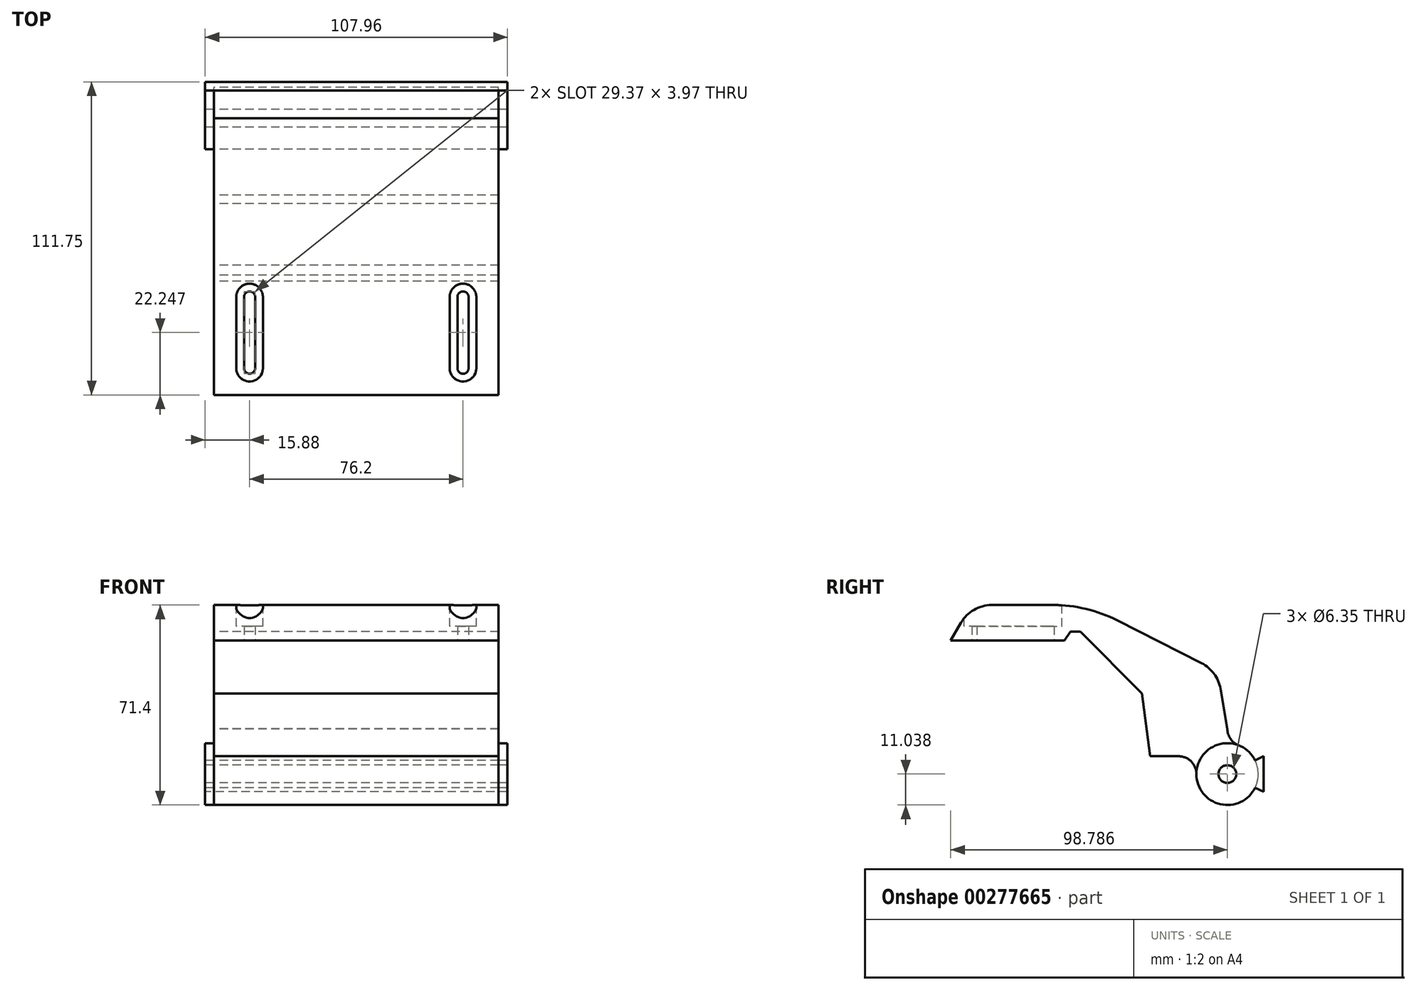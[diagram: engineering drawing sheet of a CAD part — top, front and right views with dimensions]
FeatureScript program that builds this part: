
annotation { "Feature Type Name" : "Feature", "Feature Type Description" : "" }
export const myFeature = defineFeature(function(context is Context, id is Id, definition is map)
    precondition{}
    {
        {
            var Q0;
            Q0=qCreatedBy(makeId("Right.planeOp"),FACE);
            var sketch = newSketch(context, id + "F0", { "sketchPlane" : qUnion([Q0])});
            skLineSegment(sketch, "E0", {"start": v(-105.67, 0) * mm, "end": v(-65.03, 0) * mm});
            skLineSegment(sketch, "E1", {"start": v(-65.03, 0) * mm, "end": v(-62.9, 3.18) * mm});
            skLineSegment(sketch, "E2", {"start": v(-62.9, 3.18) * mm, "end": v(-59.37, 3.18) * mm});
            skLineSegment(sketch, "E3", {"start": v(-59.37, 3.18) * mm, "end": v(-37.35, -18.84) * mm});
            skLineSegment(sketch, "E4", {"start": v(-37.35, -18.84) * mm, "end": v(-34.4, -41.3) * mm});
            skSolve(sketch);
        }
        {
            var Q0;
            Q0=sQuery(id+"F0.wireOp",EDGE,"E0");
            var Q1;
            Q1=sQuery(id+"F0.wireOp",EDGE,"E1");
            var Q2;
            Q2=sQuery(id+"F0.wireOp",EDGE,"E2");
            var Q3;
            Q3=sQuery(id+"F0.wireOp",EDGE,"E3");
            var Q4;
            Q4=sQuery(id+"F0.wireOp",EDGE,"E4");
            extrude(context, id + "F1", {"bodyType" : ToolBodyType.SURFACE, "surfaceEntities" : qUnion([Q0, Q1, Q2, Q3, Q4]), "depth" : 73.02 * mm, "hasSecondDirection" : true, "secondDirectionOppositeDirection" : true, "secondDirectionDepth" : 73.02 * mm});
        }
        {
            var Q0;
            Q0=qCreatedBy(makeId("Right.planeOp"),FACE);
            var sketch = newSketch(context, id + "F2", { "sketchPlane" : qUnion([Q0])});
            skLineSegment(sketch, "E5.0", {"start": v(-105.67, 0) * mm, "end": v(-65.03, 0) * mm});
            skLineSegment(sketch, "E6", {"start": v(-105.67, 0) * mm, "end": v(-98.34, 12.7) * mm});
            skLineSegment(sketch, "E7", {"start": v(-98.34, 12.7) * mm, "end": v(-57.06, 12.7) * mm});
            skLineSegment(sketch, "E8", {"start": v(-57.06, 12.7) * mm, "end": v(-10.39, -10.96) * mm});
            skLineSegment(sketch, "E9.0.0", {"start": v(-62.9, 3.18) * mm, "end": v(-65.03, 0) * mm});
            skLineSegment(sketch, "E9.0.2", {"start": v(-65.03, 0) * mm, "end": v(-62.9, 3.18) * mm});
            skLineSegment(sketch, "E10.0.0", {"start": v(-59.37, 3.18) * mm, "end": v(-62.9, 3.18) * mm});
            skLineSegment(sketch, "E10.0.2", {"start": v(-62.9, 3.18) * mm, "end": v(-59.37, 3.18) * mm});
            skLineSegment(sketch, "E11.0.0", {"start": v(-37.35, -18.84) * mm, "end": v(-59.37, 3.18) * mm});
            skLineSegment(sketch, "E11.0.2", {"start": v(-59.37, 3.18) * mm, "end": v(-37.35, -18.84) * mm});
            skLineSegment(sketch, "E12.0.0", {"start": v(-34.4, -41.3) * mm, "end": v(-37.35, -18.84) * mm});
            skLineSegment(sketch, "E12.0.2", {"start": v(-37.35, -18.84) * mm, "end": v(-34.4, -41.3) * mm});
            skLineSegment(sketch, "E13", {"start": v(-34.4, -41.3) * mm, "end": v(-21.7, -41.3) * mm});
            skArc(sketch, "E14", {"start": v(-6.88, -31.54) * mm, "mid": v(-15.75, -34.2) * mm, "end": v(-21.7, -41.3) * mm});
            skLineSegment(sketch, "E15", {"start": v(-6.88, -31.54) * mm, "end": v(-10.39, -10.96) * mm});
            skSolve(sketch);
        }
        {
            var Q0;
            Q0 = qSketchRegion(id + "F2", true);
            extrude(context, id + "F3", {"entities" : qUnion([Q0]), "endBound" : BoundingType.SYMMETRIC, "depth" : 101.6 * mm});
        }
        {
            var Q0;
            Q0=qCreatedBy(makeId("Right.planeOp"),FACE);
            var sketch = newSketch(context, id + "F4", { "sketchPlane" : qUnion([Q0])});
            skArc(sketch, "E16.0", {"start": v(-6.88, -31.54) * mm, "mid": v(-15.75, -34.2) * mm, "end": v(-21.7, -41.3) * mm});
            skLineSegment(sketch, "E17", {"start": v(-6.88, -31.47) * mm, "end": v(-6.88, -31.54) * mm});
            skLineSegment(sketch, "E18", {"start": v(-24.27, -41.3) * mm, "end": v(-21.7, -41.3) * mm});
            skArc(sketch, "E19", {"start": v(-17.92, -47.66) * mm, "mid": v(-0.67, -56.78) * mm, "end": v(-2.85, -37.39) * mm});
            skCircle(sketch, "E20", {"center": v(-6.88, -47.66) * mm, "radius": 3.18 * mm});
            skPoint(sketch, "E21.visualSharp", {"position": v(-6.88, -36.62) * mm});
            skArc(sketch, "E21.filletArc", {"start": v(-6.88, -31.47) * mm, "mid": v(-5.78, -35.05) * mm, "end": v(-2.85, -37.39) * mm});
            skPoint(sketch, "E22.visualSharp", {"position": v(-15.91, -41.3) * mm});
            skArc(sketch, "E22.filletArc", {"start": v(-17.92, -47.66) * mm, "mid": v(-19.78, -43.17) * mm, "end": v(-24.27, -41.3) * mm});
            skSolve(sketch);
        }
        {
            var Q0;
            Q0=makeQuery(id+"F4.imprint","IMPRINT",FACE,{"disambiguationData":[TD([[makeQuery(id+"F4.imprint","IMPRINT",EDGE,{"derivedFrom":sQuery(id+"F4.wireOp",EDGE,"E16.0")}),1.0]])]});
            var Q1;
            Q1=makeQuery(id+"F3.opExtrude","CAP_FACE",FACE,{"disambiguationData":[OSD([sQuery(id+"F2.wireOp",EDGE,"E5.0"),sQuery(id+"F2.wireOp",EDGE,"E6"),sQuery(id+"F2.wireOp",EDGE,"E7"),sQuery(id+"F2.wireOp",EDGE,"E8"),sQuery(id+"F2.wireOp",EDGE,"E9.0.2"),sQuery(id+"F2.wireOp",EDGE,"E10.0.2"),sQuery(id+"F2.wireOp",EDGE,"E11.0.2"),sQuery(id+"F2.wireOp",EDGE,"E12.0.2"),sQuery(id+"F2.wireOp",EDGE,"E13"),sQuery(id+"F2.wireOp",EDGE,"E14"),sQuery(id+"F2.wireOp",EDGE,"E15")])],"isStart":false});
            var Q2;
            Q2=makeQuery(id+"F3.opExtrude","CAP_FACE",FACE,{"disambiguationData":[OSD([sQuery(id+"F2.wireOp",EDGE,"E5.0"),sQuery(id+"F2.wireOp",EDGE,"E6"),sQuery(id+"F2.wireOp",EDGE,"E7"),sQuery(id+"F2.wireOp",EDGE,"E8"),sQuery(id+"F2.wireOp",EDGE,"E9.0.2"),sQuery(id+"F2.wireOp",EDGE,"E10.0.2"),sQuery(id+"F2.wireOp",EDGE,"E11.0.2"),sQuery(id+"F2.wireOp",EDGE,"E12.0.2"),sQuery(id+"F2.wireOp",EDGE,"E13"),sQuery(id+"F2.wireOp",EDGE,"E14"),sQuery(id+"F2.wireOp",EDGE,"E15")])],"isStart":true});
            extrude(context, id + "F5", {"entities" : qUnion([Q0]), "operationType" : NewBodyOperationType.ADD, "endBound" : BoundingType.UP_TO_SURFACE, "endBoundEntityFace" : qUnion([Q1]), "depth" : 25.4 * mm, "hasSecondDirection" : true, "secondDirectionBound" : SecondDirectionBoundingType.UP_TO_SURFACE, "secondDirectionOppositeDirection" : true, "secondDirectionBoundEntityFace" : qUnion([Q2]), "secondDirectionDepth" : 25.4 * mm});
        }
        {
            var Q0;
            Q0=makeQuery(id+"F3.opExtrude","SWEPT_EDGE",EDGE,{"disambiguationData":[OSD([sQuery(id+"F2.wireOp",EDGE,"E7"),sQuery(id+"F2.wireOp",EDGE,"E8")])]});
            fillet(context, id + "F6", {"entities" : qUnion([Q0]), "radius" : 50.8 * mm, "tangentPropagation" : true, "allowEdgeOverflow" : false});
        }
        {
            var Q0;
            Q0=makeQuery(id+"F3.opExtrude","SWEPT_EDGE",EDGE,{"disambiguationData":[OSD([sQuery(id+"F2.wireOp",EDGE,"E6"),sQuery(id+"F2.wireOp",EDGE,"E7")])]});
            var Q1;
            Q1=makeQuery(id+"F3.opExtrude","SWEPT_EDGE",EDGE,{"disambiguationData":[OSD([sQuery(id+"F2.wireOp",EDGE,"E8"),sQuery(id+"F2.wireOp",EDGE,"E15")])]});
            fillet(context, id + "F7", {"entities" : qUnion([Q0, Q1]), "radius" : 12.7 * mm, "tangentPropagation" : true, "allowEdgeOverflow" : false});
        }
        {
            var Q0;
            Q0=makeQuery(id+"F3.opExtrude","SWEPT_FACE",FACE,{"disambiguationData":[OSD([sQuery(id+"F2.wireOp",EDGE,"E5.0")])]});
            var sketch = newSketch(context, id + "F8", { "sketchPlane" : qUnion([Q0])});
            skLineSegment(sketch, "E23", {"start": v(0, 105.67) * mm, "end": v(0, 65.03) * mm, "construction": true});
            skLineSegment(sketch, "E24", {"start": v(-38.1, 70.72) * mm, "end": v(-38.1, 96.12) * mm, "construction": true});
            skArc(sketch, "E25", {"start": v(-40.08, 70.72) * mm, "mid": v(-38.1, 68.74) * mm, "end": v(-36.12, 70.72) * mm});
            skArc(sketch, "E26", {"start": v(-36.12, 96.12) * mm, "mid": v(-38.16, 98.1) * mm, "end": v(-40.08, 96) * mm});
            skLineSegment(sketch, "E27", {"start": v(-36.12, 70.72) * mm, "end": v(-36.12, 96.12) * mm});
            skLineSegment(sketch, "E28", {"start": v(-40.08, 96.24) * mm, "end": v(-40.08, 70.72) * mm});
            skLineSegment(sketch, "E29.MirrorCS", {"start": v(36.12, 70.72) * mm, "end": v(36.12, 96.12) * mm});
            skArc(sketch, "E30.MirrorCS", {"start": v(36.12, 96.12) * mm, "mid": v(38.16, 98.1) * mm, "end": v(40.08, 96) * mm});
            skLineSegment(sketch, "E31.MirrorCS", {"start": v(40.08, 96.24) * mm, "end": v(40.08, 70.72) * mm});
            skArc(sketch, "E32.MirrorCS", {"start": v(40.08, 70.72) * mm, "mid": v(38.1, 68.74) * mm, "end": v(36.12, 70.72) * mm});
            skLineSegment(sketch, "E33.MirrorCS", {"start": v(38.1, 70.72) * mm, "end": v(38.1, 96.12) * mm, "construction": true});
            skSolve(sketch);
        }
        {
            var Q0;
            {var subQ4=sQuery(id+"F8.wireOp",EDGE,"E29.MirrorCS");Q0=makeQuery(id+"F8.imprint","IMPRINT",FACE,{"disambiguationData":[TD([[makeQuery(id+"F8.imprint","IMPRINT",EDGE,{"derivedFrom":subQ4}),-1.0]])]});}
            var Q1;
            {var subQ5=sQuery(id+"F8.wireOp",EDGE,"E25");Q1=makeQuery(id+"F8.imprint","IMPRINT",FACE,{"disambiguationData":[TD([[makeQuery(id+"F8.imprint","IMPRINT",EDGE,{"derivedFrom":subQ5}),1.0]])]});}
            extrude(context, id + "F9", {"entities" : qUnion([Q0, Q1]), "operationType" : NewBodyOperationType.REMOVE, "endBound" : BoundingType.UP_TO_NEXT, "oppositeDirection" : true, "depth" : 25.4 * mm});
        }
        {
            var Q0;
            {var subQ0=sQuery(id+"F2.wireOp",EDGE,"E7");Q0=makeQuery(id+"F9.boolean.opBoolean","SPLIT",FACE,{"disambiguationData":[TD([makeQuery(id+"F9.opExtrude","SWEPT_FACE",FACE,{"disambiguationData":[OSD([sQuery(id+"F8.wireOp",EDGE,"E27")])]})])],"derivedFrom":makeQuery(id+"F3.opExtrude","SWEPT_FACE",FACE,{"disambiguationData":[OSD([subQ0])]})});}
            var sketch = newSketch(context, id + "F10", { "sketchPlane" : qUnion([Q0])});
            skArc(sketch, "E34.0", {"start": v(-36.12, -96.12) * mm, "mid": v(-38.04, -98.1) * mm, "end": v(-40.08, -96.24) * mm, "construction": true});
            skArc(sketch, "E35.0", {"start": v(40.08, -96.24) * mm, "mid": v(38.04, -98.1) * mm, "end": v(36.12, -96.12) * mm, "construction": true});
            skArc(sketch, "E36", {"start": v(-42.86, -96.12) * mm, "mid": v(-38.1, -100.89) * mm, "end": v(-33.34, -96.12) * mm});
            skArc(sketch, "E37", {"start": v(33.34, -96.12) * mm, "mid": v(38.1, -100.89) * mm, "end": v(42.86, -96.12) * mm});
            skArc(sketch, "E38.0", {"start": v(-39.38, -69.2) * mm, "mid": v(-38.1, -68.74) * mm, "end": v(-36.82, -69.2) * mm, "construction": true});
            skArc(sketch, "E39.0", {"start": v(36.82, -69.2) * mm, "mid": v(38.1, -68.74) * mm, "end": v(39.38, -69.2) * mm, "construction": true});
            skArc(sketch, "E40", {"start": v(-33.34, -70.72) * mm, "mid": v(-38.1, -65.96) * mm, "end": v(-42.86, -70.72) * mm});
            skArc(sketch, "E41", {"start": v(42.86, -70.72) * mm, "mid": v(38.1, -65.96) * mm, "end": v(33.34, -70.72) * mm});
            skLineSegment(sketch, "E42", {"start": v(42.86, -70.72) * mm, "end": v(42.86, -96.12) * mm});
            skLineSegment(sketch, "E43", {"start": v(33.34, -70.72) * mm, "end": v(33.34, -96.12) * mm});
            skLineSegment(sketch, "E44", {"start": v(-33.34, -70.72) * mm, "end": v(-33.34, -96.12) * mm});
            skLineSegment(sketch, "E45", {"start": v(-42.86, -70.72) * mm, "end": v(-42.86, -96.12) * mm});
            skSolve(sketch);
        }
        {
            var Q0;
            {var subQ12=sQuery(id+"F10.wireOp",EDGE,"E36");Q0=makeQuery(id+"F10.imprint","IMPRINT",FACE,{"disambiguationData":[TD([[makeQuery(id+"F10.imprint","IMPRINT",EDGE,{"derivedFrom":subQ12}),1.0]])]});}
            var Q1;
            {var subQ0=sQuery(id+"F2.wireOp",EDGE,"E7");var subQ1=makeQuery(id+"F3.opExtrude","SWEPT_FACE",FACE,{"disambiguationData":[OSD([subQ0])]});var subQ7=sQuery(id+"F8.wireOp",EDGE,"E25");var subQ14=makeQuery(id+"F9.boolean.opBoolean","COPY",EDGE,{"derivedFrom":makeQuery(id+"F9.opExtrude","CAP_EDGE",EDGE,{"disambiguationData":[OSD([subQ7]),topologyDisambiguationEdgeConnected([subQ1]),OD(0.0)],"isStart":false})});Q1=makeQuery(id+"F10.imprint","IMPRINT",FACE,{"disambiguationData":[TD([[makeQuery(id+"F10.imprint","IMPRINT",EDGE,{"derivedFrom":subQ14}),1.0]])]});}
            var Q2;
            {var subQ0=sQuery(id+"F2.wireOp",EDGE,"E7");var subQ1=makeQuery(id+"F3.opExtrude","SWEPT_FACE",FACE,{"disambiguationData":[OSD([subQ0])]});var subQ2=sQuery(id+"F8.wireOp",EDGE,"E29.MirrorCS");var subQ3=makeQuery(id+"F9.boolean.opBoolean","COPY",EDGE,{"derivedFrom":makeQuery(id+"F9.opExtrude","CAP_EDGE",EDGE,{"disambiguationData":[OSD([subQ2]),topologyDisambiguationEdgeConnected([subQ1])],"isStart":false})});Q2=makeQuery(id+"F10.imprint","IMPRINT",FACE,{"disambiguationData":[TD([[makeQuery(id+"F10.imprint","IMPRINT",EDGE,{"derivedFrom":subQ3}),-1.0]])]});}
            var Q3;
            {var subQ2=sQuery(id+"F10.wireOp",EDGE,"E37");Q3=makeQuery(id+"F10.imprint","IMPRINT",FACE,{"disambiguationData":[TD([[makeQuery(id+"F10.imprint","IMPRINT",EDGE,{"derivedFrom":subQ2}),1.0]])]});}
            extrude(context, id + "F11", {"entities" : qUnion([Q0, Q1, Q2, Q3]), "operationType" : NewBodyOperationType.REMOVE, "oppositeDirection" : true, "depth" : 7.62 * mm});
        }
        {
            var Q0;
            Q0=qCreatedBy(makeId("Right.planeOp"),FACE);
            var sketch = newSketch(context, id + "F12", { "sketchPlane" : qUnion([Q0])});
            skLineSegment(sketch, "E46", {"start": v(-6.88, -47.66) * mm, "end": v(30.96, -47.66) * mm, "construction": true});
            skCircle(sketch, "E47.0", {"center": v(-6.88, -47.66) * mm, "radius": 3.18 * mm});
            skLineSegment(sketch, "E48.MirrorCS", {"start": v(3.03, -52.52) * mm, "end": v(6.08, -54.01) * mm});
            skLineSegment(sketch, "E49", {"start": v(6.08, -41.31) * mm, "end": v(6.08, -54.01) * mm});
            skArc(sketch, "E50", {"start": v(3.03, -42.8) * mm, "mid": v(-17.92, -47.66) * mm, "end": v(3.03, -52.52) * mm});
            skLineSegment(sketch, "E51.trimOffspring", {"start": v(3.03, -42.8) * mm, "end": v(6.08, -41.31) * mm});
            skSolve(sketch);
        }
        {
            var Q0;
            Q0 = qSketchRegion(id + "F12", true);
            extrude(context, id + "F13", {"entities" : qUnion([Q0]), "endBound" : BoundingType.SYMMETRIC, "depth" : 107.95 * mm});
        }
        {
            var Q0;
            Q0=makeQuery(id+"F3.opExtrude","SWEPT_BODY",BODY,{"disambiguationData":[OSD([sQuery(id+"F2.wireOp",EDGE,"E5.0"),sQuery(id+"F2.wireOp",EDGE,"E6"),sQuery(id+"F2.wireOp",EDGE,"E7"),sQuery(id+"F2.wireOp",EDGE,"E8"),sQuery(id+"F2.wireOp",EDGE,"E9.0.2"),sQuery(id+"F2.wireOp",EDGE,"E10.0.2"),sQuery(id+"F2.wireOp",EDGE,"E11.0.2"),sQuery(id+"F2.wireOp",EDGE,"E12.0.2"),sQuery(id+"F2.wireOp",EDGE,"E13"),sQuery(id+"F2.wireOp",EDGE,"E14"),sQuery(id+"F2.wireOp",EDGE,"E15")])]});
            var Q1;
            Q1=makeQuery(id+"F13.opExtrude","SWEPT_BODY",BODY,{"disambiguationData":[OSD([sQuery(id+"F12.wireOp",EDGE,"E48.MirrorCS"),sQuery(id+"F12.wireOp",EDGE,"E49"),sQuery(id+"F12.wireOp",EDGE,"E50"),sQuery(id+"F12.wireOp",EDGE,"E51.trimOffspring")])]});
            booleanBodies(context, id + "F14", {"operationType" : BooleanOperationType.SUBTRACTION, "tools" : qUnion([Q0]), "targets" : qUnion([Q1]), "keepTools" : true});
        }
    });
